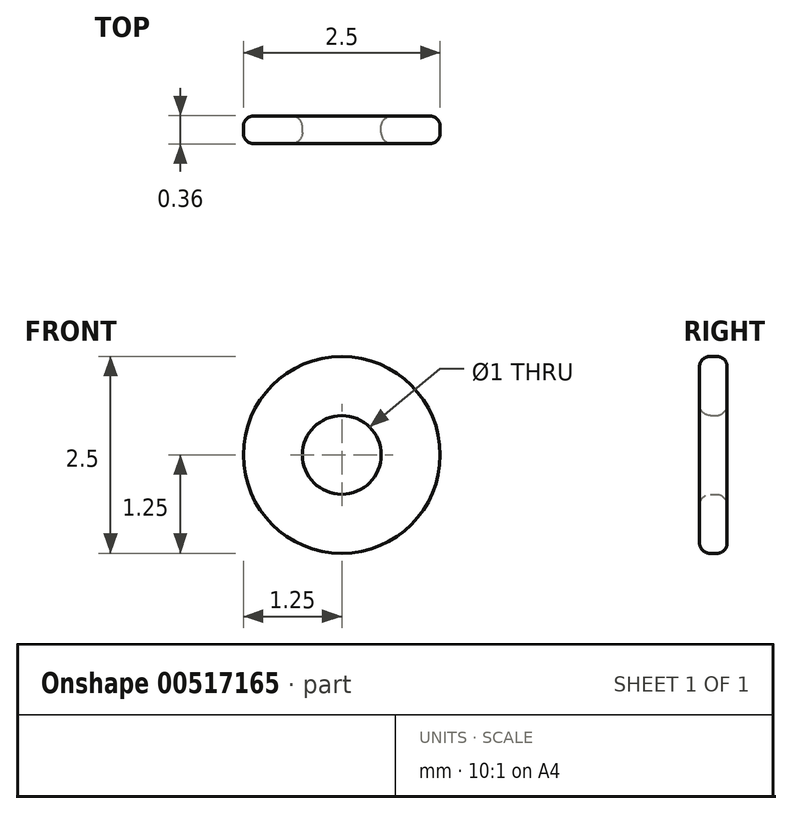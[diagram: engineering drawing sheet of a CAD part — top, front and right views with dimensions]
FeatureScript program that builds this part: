
annotation { "Feature Type Name" : "Feature", "Feature Type Description" : "" }
export const myFeature = defineFeature(function(context is Context, id is Id, definition is map)
    precondition{}
    {
        {
            var Q0;
            Q0=qCreatedBy(makeId("Front.planeOp"),FACE);
            var sketch = newSketch(context, id + "F0", { "sketchPlane" : qUnion([Q0])});
            skCircle(sketch, "E0", {"center": v(0, 0) * mm, "radius": 1.25 * mm});
            skCircle(sketch, "E1", {"center": v(0, 0) * mm, "radius": 0.5 * mm});
            skSolve(sketch);
        }
        {
            var Q0;
            Q0 = qSketchRegion(id + "F0", true);
            extrude(context, id + "F1", {"entities" : qUnion([Q0]), "endBound" : BoundingType.SYMMETRIC, "depth" : 0.35 * mm, "offsetDistance" : 25 * mm});
        }
        {
            var Q0;
            Q0=makeQuery(id+"F1.opExtrude","CAP_EDGE",EDGE,{"disambiguationData":[OSD([sQuery(id+"F0.wireOp",EDGE,"E0")])],"isStart":false});
            var Q1;
            Q1=makeQuery(id+"F1.opExtrude","CAP_EDGE",EDGE,{"disambiguationData":[OSD([sQuery(id+"F0.wireOp",EDGE,"E0")])],"isStart":true});
            fillet(context, id + "F2", {"entities" : qUnion([Q0, Q1]), "radius" : 0.13 * mm, "tangentPropagation" : true, "allowEdgeOverflow" : false});
        }
        {
            var Q0;
            Q0=makeQuery(id+"F1.opExtrude","CAP_EDGE",EDGE,{"disambiguationData":[OSD([sQuery(id+"F0.wireOp",EDGE,"E1")])],"isStart":false});
            var Q1;
            Q1=makeQuery(id+"F1.opExtrude","CAP_EDGE",EDGE,{"disambiguationData":[OSD([sQuery(id+"F0.wireOp",EDGE,"E1")])],"isStart":true});
            fillet(context, id + "F3", {"entities" : qUnion([Q0, Q1]), "radius" : 0.14 * mm, "tangentPropagation" : true, "allowEdgeOverflow" : false});
        }
    });
